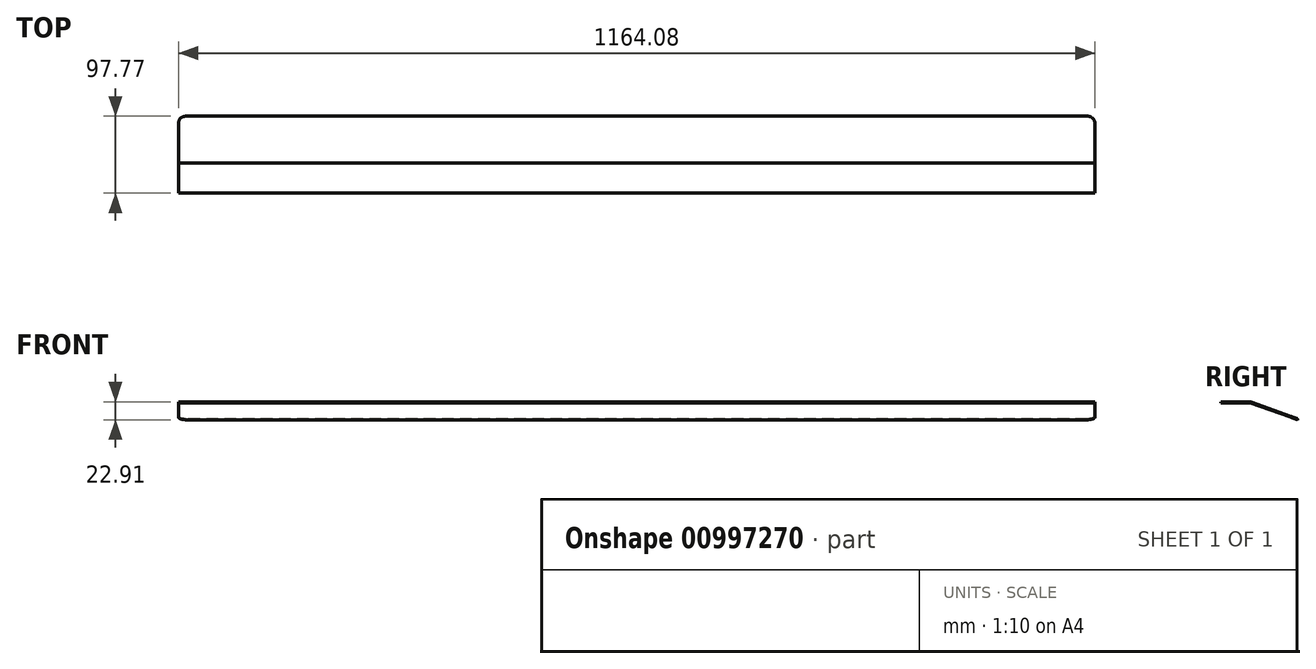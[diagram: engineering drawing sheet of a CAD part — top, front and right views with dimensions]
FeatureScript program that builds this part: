
annotation { "Feature Type Name" : "Feature", "Feature Type Description" : "" }
export const myFeature = defineFeature(function(context is Context, id is Id, definition is map)
    precondition{}
    {
        {
            var Q0;
            Q0=qCreatedBy(makeId("Right.planeOp"),FACE);
            var sketch = newSketch(context, id + "F0", { "sketchPlane" : qUnion([Q0])});
            skLineSegment(sketch, "E0", {"start": v(-33.87, 0) * mm, "end": v(4.23, 0) * mm});
            skLineSegment(sketch, "E1", {"start": v(4.23, 0) * mm, "end": v(40.04, -13.03) * mm});
            skLineSegment(sketch, "E2", {"start": v(40.04, -13.03) * mm, "end": v(63.9, -21.72) * mm});
            skLineSegment(sketch, "E3", {"start": v(63.9, -21.72) * mm, "end": v(63.47, -22.91) * mm});
            skLineSegment(sketch, "E4", {"start": v(63.47, -22.91) * mm, "end": v(37.96, -13.63) * mm});
            skLineSegment(sketch, "E5", {"start": v(37.96, -13.63) * mm, "end": v(4.01, -1.27) * mm});
            skLineSegment(sketch, "E6", {"start": v(4.01, -1.27) * mm, "end": v(-33.87, -1.27) * mm});
            skLineSegment(sketch, "E7", {"start": v(-33.87, -1.27) * mm, "end": v(-33.87, 0) * mm});
            skSolve(sketch);
        }
        {
            var Q0;
            Q0 = qSketchRegion(id + "F0", true);
            extrude(context, id + "F1", {"entities" : qUnion([Q0]), "endBound" : BoundingType.SYMMETRIC, "depth" : 1164.08 * mm, "offsetDistance" : 25.4 * mm});
        }
        {
            var Q0;
            Q0=makeQuery(id+"F1.opExtrude","CAP_EDGE",EDGE,{"disambiguationData":[OSD([sQuery(id+"F0.wireOp",EDGE,"E3")])],"isStart":false});
            fillet(context, id + "F2", {"entities" : qUnion([Q0]), "radius" : 9.52 * mm, "tangentPropagation" : true, "allowEdgeOverflow" : false});
        }
        {
            var Q0;
            Q0=makeQuery(id+"F1.opExtrude","CAP_EDGE",EDGE,{"disambiguationData":[OSD([sQuery(id+"F0.wireOp",EDGE,"E3")])],"isStart":true});
            fillet(context, id + "F3", {"entities" : qUnion([Q0]), "radius" : 9.52 * mm, "tangentPropagation" : true, "allowEdgeOverflow" : false});
        }
    });
